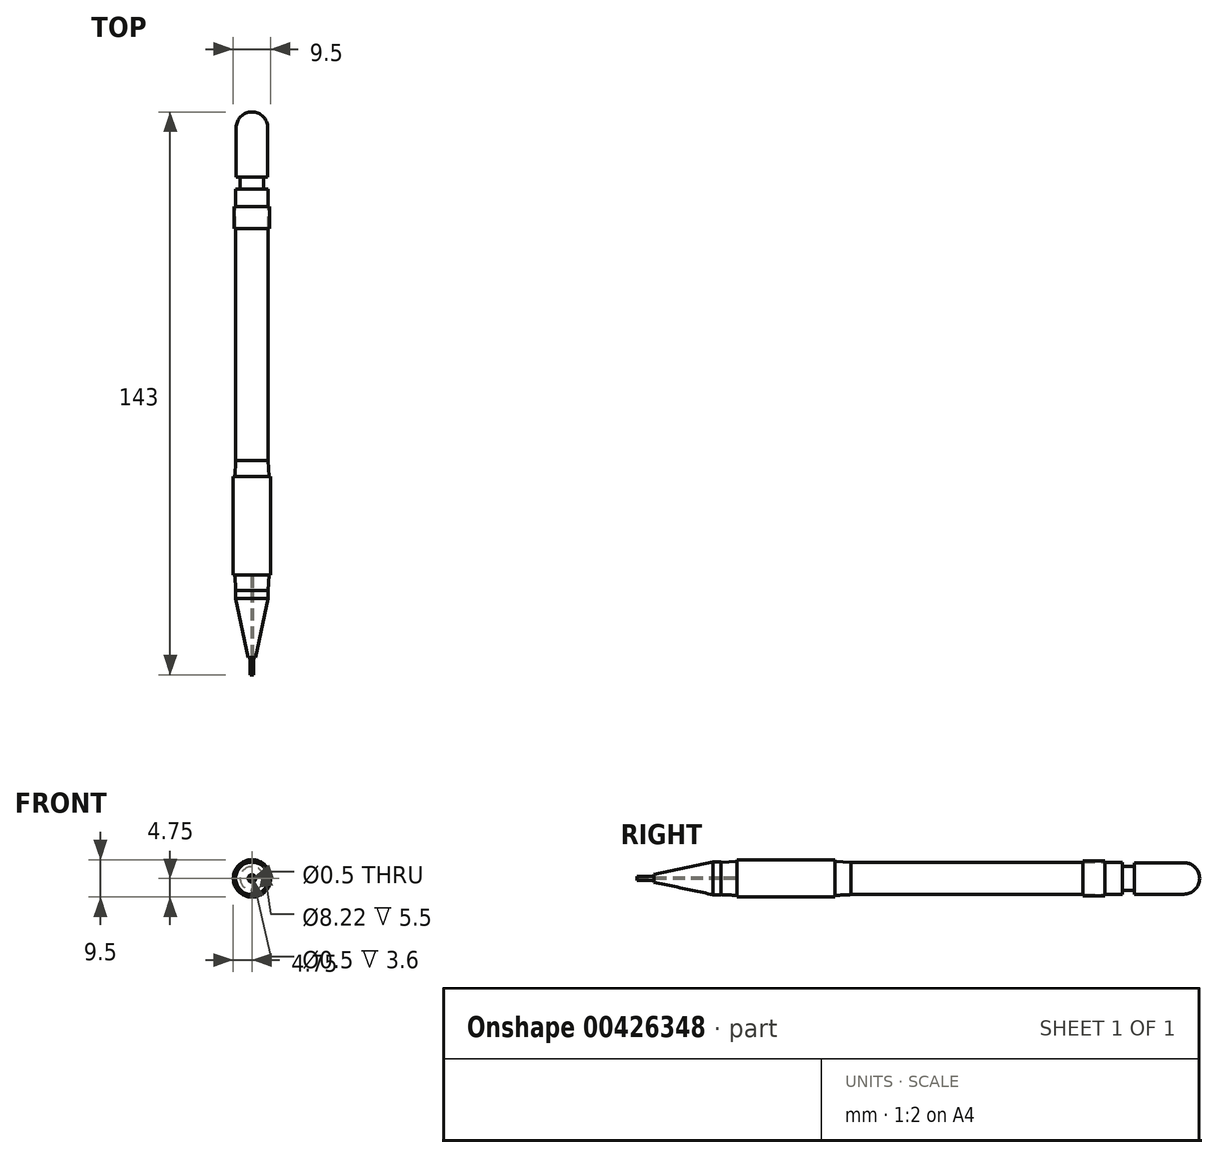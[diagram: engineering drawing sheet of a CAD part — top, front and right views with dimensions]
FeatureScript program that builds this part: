
annotation { "Feature Type Name" : "Feature", "Feature Type Description" : "" }
export const myFeature = defineFeature(function(context is Context, id is Id, definition is map)
    precondition{}
    {
        {
            var Q0;
            Q0=qCreatedBy(makeId("Front.planeOp"),FACE);
            var sketch = newSketch(context, id + "F0", { "sketchPlane" : qUnion([Q0])});
            skCircle(sketch, "E0", {"center": v(0, 0) * mm, "radius": 4.11 * mm});
            skSolve(sketch);
        }
        {
            var Q0;
            Q0=qSketchRegion(id+"F0",true);
            extrude(context, id + "F1", {"entities" : qUnion([Q0]), "depth" : 69 * mm});
        }
        {
            var Q0;
            Q0=makeQuery(id+"F1.opExtrude","CAP_FACE",FACE,{"disambiguationData":[OSD([sQuery(id+"F0.wireOp",EDGE,"E0")])],"isStart":true});
            var sketch = newSketch(context, id + "F2", { "sketchPlane" : qUnion([Q0])});
            skCircle(sketch, "E1", {"center": v(0, 0) * mm, "radius": 3 * mm});
            skSolve(sketch);
        }
        {
            var Q0;
            Q0=qSketchRegion(id+"F2",true);
            extrude(context, id + "F3", {"entities" : qUnion([Q0]), "depth" : 3 * mm});
        }
        {
            var Q0;
            Q0=makeQuery(id+"F3.opExtrude","CAP_FACE",FACE,{"disambiguationData":[OSD([sQuery(id+"F2.wireOp",EDGE,"E1")])],"isStart":false});
            var sketch = newSketch(context, id + "F4", { "sketchPlane" : qUnion([Q0])});
            skCircle(sketch, "E2", {"center": v(0, 0) * mm, "radius": 4 * mm});
            skSolve(sketch);
        }
        {
            var Q0;
            Q0=qSketchRegion(id+"F4",true);
            extrude(context, id + "F5", {"entities" : qUnion([Q0]), "depth" : 16.6 * mm});
        }
        {
            var Q0;
            Q0=makeQuery(id+"F5.opExtrude","CAP_FACE",FACE,{"disambiguationData":[OSD([sQuery(id+"F4.wireOp",EDGE,"E2")])],"isStart":false});
            fillet(context, id + "F6", {"entities" : qUnion([Q0]), "radius" : 4 * mm, "tangentPropagation" : true, "allowEdgeOverflow" : false});
        }
        {
            var Q0;
            Q0=makeQuery(id+"F1.opExtrude","CAP_FACE",FACE,{"disambiguationData":[OSD([sQuery(id+"F0.wireOp",EDGE,"E0")])],"isStart":false});
            var sketch = newSketch(context, id + "F7", { "sketchPlane" : qUnion([Q0])});
            skCircle(sketch, "E3", {"center": v(0, 0) * mm, "radius": 4.11 * mm});
            skSolve(sketch);
        }
        {
            var Q0;
            Q0=qSketchRegion(id+"F7",true);
            extrude(context, id + "F8", {"entities" : qUnion([Q0]), "depth" : 4 * mm, "hasDraft" : true, "draftAngle" : 3 * degree});
        }
        {
            var Q0;
            Q0=makeQuery(id+"F8.opExtrude","CAP_FACE",FACE,{"disambiguationData":[OSD([sQuery(id+"F7.wireOp",EDGE,"E3")])],"isStart":false});
            var sketch = newSketch(context, id + "F9", { "sketchPlane" : qUnion([Q0])});
            skCircle(sketch, "E4", {"center": v(0, 0) * mm, "radius": 4.75 * mm});
            skSolve(sketch);
        }
        {
            var Q0;
            Q0=qSketchRegion(id+"F9",true);
            extrude(context, id + "F10", {"entities" : qUnion([Q0]), "operationType" : NewBodyOperationType.ADD, "depth" : 25 * mm});
        }
        {
            var Q0;
            Q0=makeQuery(id+"F10.opExtrude","CAP_FACE",FACE,{"disambiguationData":[OSD([sQuery(id+"F9.wireOp",EDGE,"E4")])],"isStart":false});
            var sketch = newSketch(context, id + "F11", { "sketchPlane" : qUnion([Q0])});
            skCircle(sketch, "E5", {"center": v(0, 0) * mm, "radius": 4.32 * mm});
            skSolve(sketch);
        }
        {
            var Q0;
            Q0=qSketchRegion(id+"F11",true);
            extrude(context, id + "F12", {"entities" : qUnion([Q0]), "operationType" : NewBodyOperationType.ADD, "depth" : 4 * mm, "hasDraft" : true, "draftAngle" : 3 * degree, "draftPullDirection" : true});
        }
        {
            var Q0;
            Q0=makeQuery(id+"F10.opExtrude","CAP_FACE",FACE,{"disambiguationData":[OSD([sQuery(id+"F9.wireOp",EDGE,"E4")])],"isStart":true});
            var sketch = newSketch(context, id + "F13", { "sketchPlane" : qUnion([Q0])});
            skPoint(sketch, "E6.visualSharp", {"position": v(0.5, -4.72) * mm});
            skPoint(sketch, "E7.visualSharp", {"position": v(-0.5, -4.72) * mm});
            skLineSegment(sketch, "E8", {"start": v(0.5, -4.3) * mm, "end": v(0.5, -4.44) * mm});
            skLineSegment(sketch, "E9", {"start": v(-0.5, -4.3) * mm, "end": v(-0.5, -4.44) * mm});
            skArc(sketch, "E10", {"start": v(0.5, -4.3) * mm, "mid": v(0, -4.32) * mm, "end": v(-0.5, -4.3) * mm});
            skArc(sketch, "E11.filletArc", {"start": v(0.5, -4.44) * mm, "mid": v(0.59, -4.63) * mm, "end": v(0.8, -4.68) * mm});
            skArc(sketch, "E12.filletArc", {"start": v(-0.8, -4.68) * mm, "mid": v(-0.59, -4.63) * mm, "end": v(-0.5, -4.44) * mm});
            skArc(sketch, "E13", {"start": v(0.8, -4.68) * mm, "mid": v(0, -4.75) * mm, "end": v(-0.8, -4.68) * mm});
            skPoint(sketch, "E14.1.0", {"position": v(3.84, -2.8) * mm});
            skArc(sketch, "E14.1.1", {"start": v(4.1, -1.79) * mm, "mid": v(4.3, -1.8) * mm, "end": v(4.45, -1.66) * mm});
            skArc(sketch, "E14.1.2", {"start": v(3.66, -3.03) * mm, "mid": v(3.71, -2.82) * mm, "end": v(3.6, -2.65) * mm});
            skPoint(sketch, "E14.1.3", {"position": v(4.34, -1.93) * mm});
            skArc(sketch, "E14.1.4", {"start": v(4.45, -1.66) * mm, "mid": v(4.11, -2.37) * mm, "end": v(3.66, -3.03) * mm});
            skArc(sketch, "E14.1.5", {"start": v(3.97, -1.71) * mm, "mid": v(3.74, -2.16) * mm, "end": v(3.47, -2.58) * mm});
            skPoint(sketch, "E14.1.6", {"position": v(3.84, -2.8) * mm});
            skPoint(sketch, "E14.1.7", {"position": v(4.34, -1.93) * mm});
            skLineSegment(sketch, "E14.1.8", {"start": v(3.97, -1.71) * mm, "end": v(4.1, -1.79) * mm});
            skLineSegment(sketch, "E14.1.9", {"start": v(3.47, -2.58) * mm, "end": v(3.6, -2.65) * mm});
            skPoint(sketch, "E14.2.0", {"position": v(4.34, 1.93) * mm});
            skArc(sketch, "E14.2.1", {"start": v(3.6, 2.65) * mm, "mid": v(3.71, 2.82) * mm, "end": v(3.66, 3.03) * mm});
            skArc(sketch, "E14.2.2", {"start": v(4.45, 1.66) * mm, "mid": v(4.3, 1.8) * mm, "end": v(4.1, 1.79) * mm});
            skPoint(sketch, "E14.2.3", {"position": v(3.84, 2.8) * mm});
            skArc(sketch, "E14.2.4", {"start": v(3.66, 3.03) * mm, "mid": v(4.11, 2.38) * mm, "end": v(4.45, 1.66) * mm});
            skArc(sketch, "E14.2.5", {"start": v(3.47, 2.58) * mm, "mid": v(3.74, 2.16) * mm, "end": v(3.97, 1.71) * mm});
            skPoint(sketch, "E14.2.6", {"position": v(4.34, 1.93) * mm});
            skPoint(sketch, "E14.2.7", {"position": v(3.84, 2.8) * mm});
            skLineSegment(sketch, "E14.2.8", {"start": v(3.47, 2.58) * mm, "end": v(3.6, 2.65) * mm});
            skLineSegment(sketch, "E14.2.9", {"start": v(3.97, 1.71) * mm, "end": v(4.1, 1.79) * mm});
            skPoint(sketch, "E14.3.0", {"position": v(0.5, 4.72) * mm});
            skArc(sketch, "E14.3.1", {"start": v(-0.5, 4.44) * mm, "mid": v(-0.59, 4.63) * mm, "end": v(-0.8, 4.68) * mm});
            skArc(sketch, "E14.3.2", {"start": v(0.8, 4.68) * mm, "mid": v(0.59, 4.63) * mm, "end": v(0.5, 4.44) * mm});
            skPoint(sketch, "E14.3.3", {"position": v(-0.5, 4.72) * mm});
            skArc(sketch, "E14.3.4", {"start": v(-0.8, 4.68) * mm, "mid": v(0, 4.75) * mm, "end": v(0.8, 4.68) * mm});
            skArc(sketch, "E14.3.5", {"start": v(-0.5, 4.3) * mm, "mid": v(0, 4.32) * mm, "end": v(0.5, 4.3) * mm});
            skPoint(sketch, "E14.3.6", {"position": v(0.5, 4.72) * mm});
            skPoint(sketch, "E14.3.7", {"position": v(-0.5, 4.72) * mm});
            skLineSegment(sketch, "E14.3.8", {"start": v(-0.5, 4.3) * mm, "end": v(-0.5, 4.44) * mm});
            skLineSegment(sketch, "E14.3.9", {"start": v(0.5, 4.3) * mm, "end": v(0.5, 4.44) * mm});
            skPoint(sketch, "E14.4.0", {"position": v(-3.84, 2.8) * mm});
            skArc(sketch, "E14.4.1", {"start": v(-4.1, 1.79) * mm, "mid": v(-4.3, 1.8) * mm, "end": v(-4.45, 1.66) * mm});
            skArc(sketch, "E14.4.2", {"start": v(-3.66, 3.03) * mm, "mid": v(-3.71, 2.82) * mm, "end": v(-3.6, 2.65) * mm});
            skPoint(sketch, "E14.4.3", {"position": v(-4.34, 1.93) * mm});
            skArc(sketch, "E14.4.4", {"start": v(-4.45, 1.66) * mm, "mid": v(-4.11, 2.37) * mm, "end": v(-3.66, 3.03) * mm});
            skArc(sketch, "E14.4.5", {"start": v(-3.97, 1.71) * mm, "mid": v(-3.74, 2.16) * mm, "end": v(-3.47, 2.58) * mm});
            skPoint(sketch, "E14.4.6", {"position": v(-3.84, 2.8) * mm});
            skPoint(sketch, "E14.4.7", {"position": v(-4.34, 1.93) * mm});
            skLineSegment(sketch, "E14.4.8", {"start": v(-3.97, 1.71) * mm, "end": v(-4.1, 1.79) * mm});
            skLineSegment(sketch, "E14.4.9", {"start": v(-3.47, 2.58) * mm, "end": v(-3.6, 2.65) * mm});
            skPoint(sketch, "E14.5.0", {"position": v(-4.34, -1.93) * mm});
            skArc(sketch, "E14.5.1", {"start": v(-3.6, -2.65) * mm, "mid": v(-3.71, -2.82) * mm, "end": v(-3.66, -3.03) * mm});
            skArc(sketch, "E14.5.2", {"start": v(-4.45, -1.66) * mm, "mid": v(-4.3, -1.8) * mm, "end": v(-4.1, -1.79) * mm});
            skPoint(sketch, "E14.5.3", {"position": v(-3.84, -2.8) * mm});
            skArc(sketch, "E14.5.4", {"start": v(-3.66, -3.03) * mm, "mid": v(-4.11, -2.38) * mm, "end": v(-4.45, -1.66) * mm});
            skArc(sketch, "E14.5.5", {"start": v(-3.47, -2.58) * mm, "mid": v(-3.74, -2.16) * mm, "end": v(-3.97, -1.71) * mm});
            skPoint(sketch, "E14.5.6", {"position": v(-4.34, -1.93) * mm});
            skPoint(sketch, "E14.5.7", {"position": v(-3.84, -2.8) * mm});
            skLineSegment(sketch, "E14.5.8", {"start": v(-3.47, -2.58) * mm, "end": v(-3.6, -2.65) * mm});
            skLineSegment(sketch, "E14.5.9", {"start": v(-3.97, -1.71) * mm, "end": v(-4.1, -1.79) * mm});
            skSolve(sketch);
        }
        {
            var Q0;
            Q0=qCreatedBy(makeId("Right.planeOp"),FACE);
            var sketch = newSketch(context, id + "F14", { "sketchPlane" : qUnion([Q0])});
            skLineSegment(sketch, "E15", {"start": v(-75.6, -4.5) * mm, "end": v(-75.6, -4.32) * mm});
            skLineSegment(sketch, "E16", {"start": v(-77.1, -4.5) * mm, "end": v(-77.1, -4.32) * mm});
            skLineSegment(sketch, "E17", {"start": v(-75.35, -4.75) * mm, "end": v(-75.35, -4.75) * mm});
            skPoint(sketch, "E18.newPointA", {"position": v(-75.6, -4.75) * mm});
            skArc(sketch, "E18.filletArc", {"start": v(-75.6, -4.5) * mm, "mid": v(-75.53, -4.68) * mm, "end": v(-75.35, -4.75) * mm});
            skLineSegment(sketch, "E19", {"start": v(-76.85, -4.75) * mm, "end": v(-77.35, -4.75) * mm});
            skPoint(sketch, "E20.visualSharp", {"position": v(-77.1, -4.75) * mm});
            skArc(sketch, "E20.filletArc", {"start": v(-77.35, -4.75) * mm, "mid": v(-77.17, -4.68) * mm, "end": v(-77.1, -4.5) * mm});
            skLineSegment(sketch, "E21", {"start": v(-75.35, -4.75) * mm, "end": v(-77.35, -4.75) * mm});
            skLineSegment(sketch, "E22", {"start": v(-75.6, -4.32) * mm, "end": v(-77.1, -4.32) * mm});
            skLineSegment(sketch, "E23.1.0.0", {"start": v(-81.6, -4.5) * mm, "end": v(-81.6, -4.32) * mm});
            skPoint(sketch, "E23.1.0.1", {"position": v(-80.1, -4.75) * mm});
            skLineSegment(sketch, "E23.1.0.2", {"start": v(-79.85, -4.75) * mm, "end": v(-81.85, -4.75) * mm});
            skArc(sketch, "E23.1.0.3", {"start": v(-81.85, -4.75) * mm, "mid": v(-81.67, -4.68) * mm, "end": v(-81.6, -4.5) * mm});
            skPoint(sketch, "E23.1.0.4", {"position": v(-81.6, -4.75) * mm});
            skLineSegment(sketch, "E23.1.0.5", {"start": v(-80.1, -4.32) * mm, "end": v(-81.6, -4.32) * mm});
            skLineSegment(sketch, "E23.1.0.6", {"start": v(-80.1, -4.5) * mm, "end": v(-80.1, -4.32) * mm});
            skArc(sketch, "E23.1.0.7", {"start": v(-80.1, -4.5) * mm, "mid": v(-80.03, -4.68) * mm, "end": v(-79.85, -4.75) * mm});
            skLineSegment(sketch, "E23.1.0.8", {"start": v(-81.35, -4.75) * mm, "end": v(-81.85, -4.75) * mm});
            skLineSegment(sketch, "E23.2.0.0", {"start": v(-86.1, -4.5) * mm, "end": v(-86.1, -4.32) * mm});
            skPoint(sketch, "E23.2.0.1", {"position": v(-84.6, -4.75) * mm});
            skLineSegment(sketch, "E23.2.0.2", {"start": v(-84.35, -4.75) * mm, "end": v(-86.35, -4.75) * mm});
            skArc(sketch, "E23.2.0.3", {"start": v(-86.35, -4.75) * mm, "mid": v(-86.17, -4.68) * mm, "end": v(-86.1, -4.5) * mm});
            skPoint(sketch, "E23.2.0.4", {"position": v(-86.1, -4.75) * mm});
            skLineSegment(sketch, "E23.2.0.5", {"start": v(-84.6, -4.32) * mm, "end": v(-86.1, -4.32) * mm});
            skLineSegment(sketch, "E23.2.0.6", {"start": v(-84.6, -4.5) * mm, "end": v(-84.6, -4.32) * mm});
            skArc(sketch, "E23.2.0.7", {"start": v(-84.6, -4.5) * mm, "mid": v(-84.53, -4.68) * mm, "end": v(-84.35, -4.75) * mm});
            skLineSegment(sketch, "E23.2.0.8", {"start": v(-85.85, -4.75) * mm, "end": v(-86.35, -4.75) * mm});
            skLineSegment(sketch, "E23.3.0.0", {"start": v(-90.6, -4.5) * mm, "end": v(-90.6, -4.32) * mm});
            skPoint(sketch, "E23.3.0.1", {"position": v(-89.1, -4.75) * mm});
            skLineSegment(sketch, "E23.3.0.2", {"start": v(-88.85, -4.75) * mm, "end": v(-90.85, -4.75) * mm});
            skArc(sketch, "E23.3.0.3", {"start": v(-90.85, -4.75) * mm, "mid": v(-90.67, -4.68) * mm, "end": v(-90.6, -4.5) * mm});
            skPoint(sketch, "E23.3.0.4", {"position": v(-90.6, -4.75) * mm});
            skLineSegment(sketch, "E23.3.0.5", {"start": v(-89.1, -4.32) * mm, "end": v(-90.6, -4.32) * mm});
            skLineSegment(sketch, "E23.3.0.6", {"start": v(-89.1, -4.5) * mm, "end": v(-89.1, -4.32) * mm});
            skArc(sketch, "E23.3.0.7", {"start": v(-89.1, -4.5) * mm, "mid": v(-89.03, -4.68) * mm, "end": v(-88.85, -4.75) * mm});
            skLineSegment(sketch, "E23.3.0.8", {"start": v(-90.35, -4.75) * mm, "end": v(-90.85, -4.75) * mm});
            skLineSegment(sketch, "E23.4.0.0", {"start": v(-95.1, -4.5) * mm, "end": v(-95.1, -4.32) * mm});
            skPoint(sketch, "E23.4.0.1", {"position": v(-93.6, -4.75) * mm});
            skLineSegment(sketch, "E23.4.0.2", {"start": v(-93.35, -4.75) * mm, "end": v(-95.35, -4.75) * mm});
            skArc(sketch, "E23.4.0.3", {"start": v(-95.35, -4.75) * mm, "mid": v(-95.17, -4.68) * mm, "end": v(-95.1, -4.5) * mm});
            skPoint(sketch, "E23.4.0.4", {"position": v(-95.1, -4.75) * mm});
            skLineSegment(sketch, "E23.4.0.5", {"start": v(-93.6, -4.32) * mm, "end": v(-95.1, -4.32) * mm});
            skLineSegment(sketch, "E23.4.0.6", {"start": v(-93.6, -4.5) * mm, "end": v(-93.6, -4.32) * mm});
            skArc(sketch, "E23.4.0.7", {"start": v(-93.6, -4.5) * mm, "mid": v(-93.53, -4.68) * mm, "end": v(-93.35, -4.75) * mm});
            skLineSegment(sketch, "E23.4.0.8", {"start": v(-94.85, -4.75) * mm, "end": v(-95.35, -4.75) * mm});
            skLineSegment(sketch, "E23.direction1", {"start": v(-77.35, -4.75) * mm, "end": v(-81.85, -4.75) * mm, "construction": true});
            skLineSegment(sketch, "E24", {"start": v(-73.25, -4.75) * mm, "end": v(-73, -4.75) * mm});
            skLineSegment(sketch, "E25", {"start": v(-73, -4.75) * mm, "end": v(-73, -4.5) * mm});
            skArc(sketch, "E26", {"start": v(-73.25, -4.75) * mm, "mid": v(-73.07, -4.68) * mm, "end": v(-73, -4.5) * mm});
            skLineSegment(sketch, "E27", {"start": v(-97.75, -4.75) * mm, "end": v(-98, -4.75) * mm});
            skLineSegment(sketch, "E28", {"start": v(-98, -4.75) * mm, "end": v(-98, -4.5) * mm});
            skArc(sketch, "E29", {"start": v(-98, -4.5) * mm, "mid": v(-97.93, -4.68) * mm, "end": v(-97.75, -4.75) * mm});
            skSolve(sketch);
        }
        {
            var Q0;
            Q0=makeQuery(id+"F12.opExtrude","CAP_FACE",FACE,{"disambiguationData":[OSD([sQuery(id+"F11.wireOp",EDGE,"E5")])],"isStart":false});
            var sketch = newSketch(context, id + "F15", { "sketchPlane" : qUnion([Q0])});
            skCircle(sketch, "E30", {"center": v(0, 0) * mm, "radius": 4.15 * mm});
            skSolve(sketch);
        }
        {
            var Q0;
            Q0=qSketchRegion(id+"F15",true);
            extrude(context, id + "F16", {"entities" : qUnion([Q0]), "depth" : 2 * mm});
        }
        {
            var Q0;
            Q0=makeQuery(id+"F16.opExtrude","CAP_FACE",FACE,{"disambiguationData":[OSD([sQuery(id+"F15.wireOp",EDGE,"E30")])],"isStart":false});
            var sketch = newSketch(context, id + "F17", { "sketchPlane" : qUnion([Q0])});
            skCircle(sketch, "E31", {"center": v(0, 0) * mm, "radius": 4.15 * mm});
            skSolve(sketch);
        }
        {
            var Q0;
            Q0=qSketchRegion(id+"F17",true);
            extrude(context, id + "F18", {"entities" : qUnion([Q0]), "operationType" : NewBodyOperationType.ADD, "depth" : 15 * mm, "hasDraft" : true, "draftAngle" : 12 * degree, "draftPullDirection" : true});
        }
        {
            var Q0;
            Q0=makeQuery(id+"F18.opExtrude","CAP_FACE",FACE,{"disambiguationData":[OSD([sQuery(id+"F17.wireOp",EDGE,"E31")])],"isStart":false});
            var sketch = newSketch(context, id + "F19", { "sketchPlane" : qUnion([Q0])});
            skCircle(sketch, "E32", {"center": v(0, 0) * mm, "radius": 0.47 * mm});
            skSolve(sketch);
        }
        {
            var Q0;
            Q0=qSketchRegion(id+"F19",true);
            extrude(context, id + "F20", {"entities" : qUnion([Q0]), "operationType" : NewBodyOperationType.ADD, "depth" : 4.4 * mm});
        }
        {
            var Q0;
            Q0=makeQuery(id+"F20.opExtrude","CAP_FACE",FACE,{"disambiguationData":[OSD([sQuery(id+"F19.wireOp",EDGE,"E32")])],"isStart":false});
            var sketch = newSketch(context, id + "F21", { "sketchPlane" : qUnion([Q0])});
            skCircle(sketch, "E33", {"center": v(0, 0) * mm, "radius": 0.25 * mm});
            skSolve(sketch);
        }
        {
            var Q0;
            Q0=qSketchRegion(id+"F21",true);
            extrude(context, id + "F22", {"entities" : qUnion([Q0]), "operationType" : NewBodyOperationType.REMOVE, "oppositeDirection" : true, "depth" : 25 * mm});
        }
        {
            var Q0;
            Q0=qCreatedBy(makeId("Right.planeOp"),FACE);
            var sketch = newSketch(context, id + "F23", { "sketchPlane" : qUnion([Q0])});
            skLineSegment(sketch, "E34", {"start": v(-54, -1.5) * mm, "end": v(-15, -1.5) * mm});
            skSolve(sketch);
        }
        {
            var Q0;
            Q0=makeQuery(id+"F1.opExtrude","CAP_FACE",FACE,{"disambiguationData":[OSD([sQuery(id+"F0.wireOp",EDGE,"E0")])],"isStart":true});
            cPlane(context, id + "F24", {"entities" : qUnion([Q0]), "cplaneType" : CPlaneType.OFFSET, "offset" : 4.5 * mm, "oppositeDirection" : true, "width" : 150 * mm, "height" : 150 * mm});
        }
        {
            var Q0;
            Q0=qCreatedBy(id+"F24.planeOp",FACE);
            var sketch = newSketch(context, id + "F25", { "sketchPlane" : qUnion([Q0])});
            skCircle(sketch, "E35", {"center": v(0, 0) * mm, "radius": 4.11 * mm});
            skCircle(sketch, "E36", {"center": v(0, 0) * mm, "radius": 4.5 * mm});
            skSolve(sketch);
        }
        {
            var Q0;
            Q0=qSketchRegion(id+"F25",true);
            extrude(context, id + "F26", {"entities" : qUnion([Q0]), "oppositeDirection" : true, "depth" : 5.5 * mm});
        }
        {
            var Q0;
            Q0=qCreatedBy(makeId("Top.planeOp"),FACE);
            var sketch = newSketch(context, id + "F27", { "sketchPlane" : qUnion([Q0])});
            skLineSegment(sketch, "E37.bottom", {"start": v(4.1, -4.4) * mm, "end": v(4.5, -4.4) * mm});
            skLineSegment(sketch, "E37.top", {"start": v(4.11, -1.9) * mm, "end": v(4.5, -1.9) * mm});
            skLineSegment(sketch, "E37.left", {"start": v(4.11, -4.4) * mm, "end": v(4.11, -1.9) * mm});
            skLineSegment(sketch, "E37.right", {"start": v(4.5, -4.4) * mm, "end": v(4.5, -1.9) * mm});
            skLineSegment(sketch, "E38", {"start": v(4.5, -1.9) * mm, "end": v(9.68, -1.44) * mm, "construction": true});
            skArc(sketch, "E39", {"start": v(4.11, -1.9) * mm, "mid": v(5.04, -0.9) * mm, "end": v(6.1, -1.75) * mm});
            skArc(sketch, "E40", {"start": v(4.5, -1.9) * mm, "mid": v(5.06, -1.28) * mm, "end": v(5.71, -1.78) * mm});
            skLineSegment(sketch, "E41", {"start": v(14.2, -36) * mm, "end": v(-9.24, -36) * mm, "construction": true});
            skLineSegment(sketch, "E42", {"start": v(5.71, -1.78) * mm, "end": v(5.71, -36) * mm, "construction": true});
            skLineSegment(sketch, "E43", {"start": v(6.1, -1.75) * mm, "end": v(6.1, -36) * mm, "construction": true});
            skArc(sketch, "E44", {"start": v(5.71, -1.78) * mm, "mid": v(7.2, -18.15) * mm, "end": v(5.97, -34.53) * mm});
            skArc(sketch, "E45", {"start": v(6.1, -1.75) * mm, "mid": v(7.6, -18.1) * mm, "end": v(6.38, -34.49) * mm});
            skLineSegment(sketch, "E46", {"start": v(4.11, -4.4) * mm, "end": v(4.11, -36) * mm, "construction": true});
            skLineSegment(sketch, "E47", {"start": v(4.4, -34.47) * mm, "end": v(4.15, -32.8) * mm});
            skLineSegment(sketch, "E48", {"start": v(4.74, -34.52) * mm, "end": v(4.46, -32.6) * mm});
            skArc(sketch, "E49.filletArc", {"start": v(4.74, -34.52) * mm, "mid": v(5.35, -35.05) * mm, "end": v(5.97, -34.53) * mm});
            skArc(sketch, "E50.filletArc", {"start": v(4.4, -34.47) * mm, "mid": v(5.38, -35.33) * mm, "end": v(6.38, -34.49) * mm});
            skPoint(sketch, "E51.visualSharp", {"position": v(4.11, -32.51) * mm});
            skPoint(sketch, "E52.visualSharp", {"position": v(4.31, -31.6) * mm});
            skArc(sketch, "E53", {"start": v(4.15, -32.8) * mm, "mid": v(4.2, -32) * mm, "end": v(4.57, -31.3) * mm});
            skLineSegment(sketch, "E54", {"start": v(6.04, -32.52) * mm, "end": v(4.57, -31.3) * mm, "construction": true});
            skArc(sketch, "E55", {"start": v(4.46, -32.6) * mm, "mid": v(4.54, -32.03) * mm, "end": v(4.82, -31.51) * mm});
            skLineSegment(sketch, "E56", {"start": v(4.82, -31.51) * mm, "end": v(6.1, -29.96) * mm});
            skLineSegment(sketch, "E57", {"start": v(6.1, -29.96) * mm, "end": v(5.85, -29.76) * mm});
            skLineSegment(sketch, "E58", {"start": v(5.86, -29.75) * mm, "end": v(4.57, -31.3) * mm});
            skSolve(sketch);
        }
        {
            var Q0;
            Q0=qSketchRegion(id+"F27",true);
            extrude(context, id + "F28", {"entities" : qUnion([Q0]), "operationType" : NewBodyOperationType.ADD, "depth" : 5 * mm, "symmetric" : true});
        }
        {
            var Q0;
            Q0=makeQuery(id+"F28.opExtrude","SWEPT_BODY",BODY,{"disambiguationData":[OSD([sQuery(id+"F27.wireOp",EDGE,"E37.bottom"),sQuery(id+"F27.wireOp",EDGE,"E37.left"),sQuery(id+"F27.wireOp",EDGE,"E37.right"),sQuery(id+"F27.wireOp",EDGE,"E39"),sQuery(id+"F27.wireOp",EDGE,"E40"),sQuery(id+"F27.wireOp",EDGE,"E44"),sQuery(id+"F27.wireOp",EDGE,"E45"),sQuery(id+"F27.wireOp",EDGE,"E47"),sQuery(id+"F27.wireOp",EDGE,"E48"),sQuery(id+"F27.wireOp",EDGE,"E49.filletArc"),sQuery(id+"F27.wireOp",EDGE,"E50.filletArc"),sQuery(id+"F27.wireOp",EDGE,"E53"),sQuery(id+"F27.wireOp",EDGE,"E55"),sQuery(id+"F27.wireOp",EDGE,"E56"),sQuery(id+"F27.wireOp",EDGE,"E57"),sQuery(id+"F27.wireOp",EDGE,"E58")])]});
            deleteBodies(context, id + "F29", {"entities" : qUnion([Q0])});
        }
    });
